# Revit family: 1Electronics_Community-Subwoofers_Biamp_VLF_208
name_source: partatom
category: Communication Devices
units: mm (PartAtom-declared; Revit-internal decimal feet)

## family parameters
Cut with Voids When Loaded = No
Host = Face
Maintain Annotation Orientation = No
OmniClass Number = 23.85.10.11.14.14.14
Part Type = Normal
Room Calculation Point = No
Round Connector Dimension = Use Diameter
Shared = No

## types (2) — shared parameters
Axial Q / DI = 1/0, 60 Hz to 160 Hz
Connector Description = NL4, Terminal strip; 300W continuous, 750W program, 4 ohms 35 volts RMS, 77 volts momentary peak
Default Elevation = 4' - 0"
Depth = 1' - 1"
Description = VLF208 Versatile Low Frequency Dual 8-Inch Slot-Loaded Micro Subwoofer
Driver Protection = DYNA-TECH™
Drivers = LF (2) 8 inches
Enclosure = 11-ply cross-laminated birch
Height = 0' - 8 1/2"
Input Connection = (1) NL4-compatible locking connector, (1) 2 conductor barrier strip
Loudspeaker Type = Compact subwoofer
Manufacturer = Biamp
Maximum Output = 120 dB SPL / 127 dB SPL (peak)
Minimum Impedance = 4.8 ohms @ 130 Hz
Mounting/Rigging Provisions = (8) M10 hang points
Nominal Impedance = 4 ohms
Nominal –6dB Beamwidth = 360° H x 180° V
Operating Range = 55 Hz to 400 Hz, 60 Hz to 160 Hz (±1 dB) processed
Optional Accessories = VLF-SAB steered array bracket; VLF-Y208 yoke mounting bracket
Product Documentation Link = https://downloads.biamp.com
Product Page URL = https://www.biamp.com
Product data url = https://www.bimobject.com
Recommended Power Amplifier = 630W to 900W @ 4 ohms
Recommended Signal Processing = 55 Hz high pass filter, 48 dB/Oct
Required Accessories = Digital signal processor
Sensitivity (1W/1m) = 95 dB SPL (63 Hz to 160 Hz 1/3 octave bands)
URL = https://www.biamp.com
Weight = 42.00 lbf
Width = 1' - 10"

## per-type parameters (varying)
| type | Housing Material | Material of U-bracket |
| VLF-208 B | Biamp - Plastic - Black | Biamp - Metal - Black |
| VLF-208 W | Biamp - Plastic - White | Biamp - Metal - White |

note: column(s) folded — value = type name in every type: Model

## geometry (parser evidence)
native form markers: Sweep x5
no freeform markers — native parametric forms only
